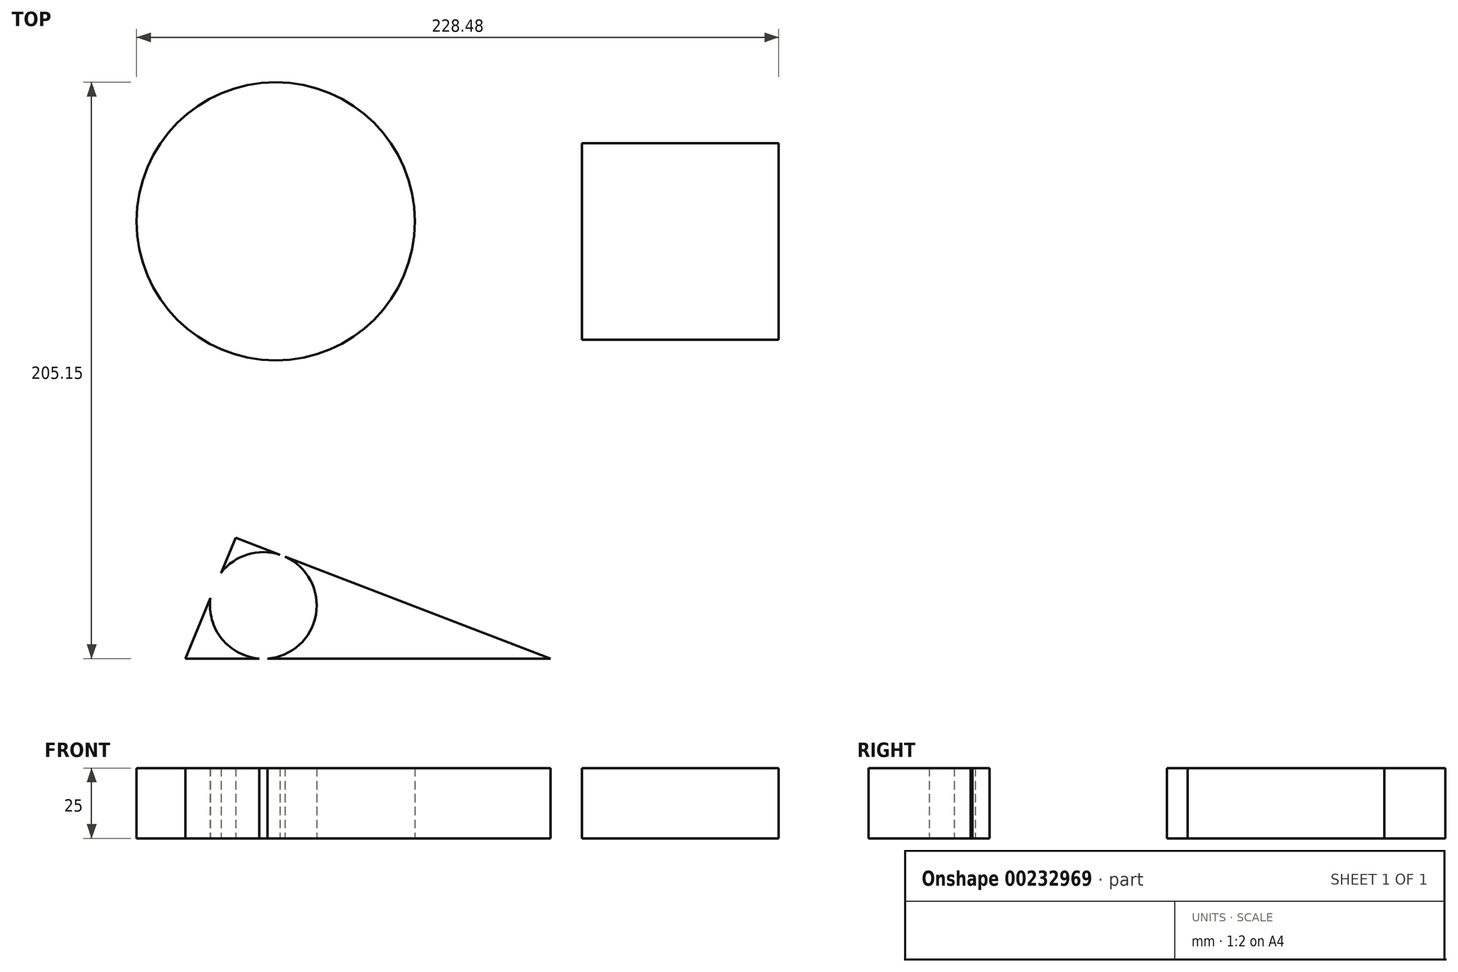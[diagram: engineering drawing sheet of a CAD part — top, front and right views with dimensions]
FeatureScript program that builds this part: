
annotation { "Feature Type Name" : "Feature", "Feature Type Description" : "" }
export const myFeature = defineFeature(function(context is Context, id is Id, definition is map)
    precondition{}
    {
        {
            var Q0;
            Q0=qCreatedBy(makeId("Top.planeOp"),FACE);
            var sketch = newSketch(context, id + "F0", { "sketchPlane" : qUnion([Q0])});
            skLineSegment(sketch, "E0.bottom", {"start": v(65.6, 3.6) * mm, "end": v(-4.4, 3.6) * mm});
            skLineSegment(sketch, "E0.top", {"start": v(65.6, 73.6) * mm, "end": v(-4.4, 73.6) * mm});
            skLineSegment(sketch, "E0.left", {"start": v(65.6, 3.6) * mm, "end": v(65.6, 73.6) * mm});
            skLineSegment(sketch, "E0.right", {"start": v(-4.4, 3.6) * mm, "end": v(-4.4, 73.6) * mm});
            skCircle(sketch, "E1", {"center": v(30.6, 38.6) * mm, "radius": 35 * mm});
            skPoint(sketch, "E1.first.point", {"position": v(30.6, 3.6) * mm});
            skPoint(sketch, "E1.second.point", {"position": v(30.6, 73.6) * mm});
            skPoint(sketch, "E1.third.point", {"position": v(65.6, 38.6) * mm});
            skLineSegment(sketch, "E2.bottom", {"start": v(-78.38, 10.8) * mm, "end": v(-148.38, 10.8) * mm});
            skLineSegment(sketch, "E2.top", {"start": v(-78.38, 80.8) * mm, "end": v(-148.38, 80.8) * mm});
            skLineSegment(sketch, "E2.left", {"start": v(-78.38, 10.8) * mm, "end": v(-78.38, 80.8) * mm});
            skLineSegment(sketch, "E2.right", {"start": v(-148.38, 10.8) * mm, "end": v(-148.38, 80.8) * mm});
            skCircle(sketch, "E3", {"center": v(-113.38, 45.8) * mm, "radius": 49.5 * mm});
            skLineSegment(sketch, "E4", {"start": v(-145.57, -109.85) * mm, "end": v(-15.57, -109.85) * mm});
            skLineSegment(sketch, "E5", {"start": v(-15.57, -109.85) * mm, "end": v(-127.6, -66.85) * mm});
            skLineSegment(sketch, "E6", {"start": v(-127.6, -66.85) * mm, "end": v(-145.57, -109.85) * mm});
            skCircle(sketch, "E7", {"center": v(-117.78, -90.92) * mm, "radius": 18.98 * mm});
            skPoint(sketch, "E7.first.point", {"position": v(-136.58, -88.35) * mm});
            skPoint(sketch, "E7.second.point", {"position": v(-98.92, -93.13) * mm});
            skPoint(sketch, "E7.third.point", {"position": v(-110.07, -73.57) * mm});
            skSolve(sketch);
        }
        {
            var Q0;
            {var subQ0=sQuery(id+"F0.wireOp",EDGE,"E2.left");Q0=makeQuery(id+"F0.imprint","IMPRINT",FACE,{"disambiguationData":[TD([[makeQuery(id+"F0.imprint","IMPRINT",EDGE,{"derivedFrom":subQ0}),-1.0]])]});}
            var Q1;
            {var subQ0=sQuery(id+"F0.wireOp",EDGE,"E2.right");Q1=makeQuery(id+"F0.imprint","IMPRINT",FACE,{"disambiguationData":[TD([[makeQuery(id+"F0.imprint","IMPRINT",EDGE,{"derivedFrom":subQ0}),1.0]])]});}
            var Q2;
            {var subQ0=sQuery(id+"F0.wireOp",EDGE,"E6");var subQ1=sQuery(id+"F0.wireOp",EDGE,"E4");var subQ2=makeQuery(id+"F0.imprint","INTERSECT",VERTEX,{"derivedFrom":[subQ1,subQ0]});Q2=makeQuery(id+"F0.imprint","IMPRINT",FACE,{"disambiguationData":[TD([[makeQuery(id+"F0.imprint","IMPRINT",EDGE,{"disambiguationData":[TD([[subQ2,-1.0]])],"derivedFrom":subQ1}),1.0]])]});}
            var Q3;
            {var subQ0=sQuery(id+"F0.wireOp",EDGE,"E5");var subQ1=sQuery(id+"F0.wireOp",EDGE,"E4");var subQ2=makeQuery(id+"F0.imprint","INTERSECT",VERTEX,{"derivedFrom":[subQ1,subQ0]});Q3=makeQuery(id+"F0.imprint","IMPRINT",FACE,{"disambiguationData":[TD([[makeQuery(id+"F0.imprint","IMPRINT",EDGE,{"disambiguationData":[TD([[subQ2,1.0]])],"derivedFrom":subQ1}),1.0]])]});}
            var Q4;
            {var subQ0=sQuery(id+"F0.wireOp",EDGE,"E6");var subQ1=sQuery(id+"F0.wireOp",EDGE,"E5");var subQ2=makeQuery(id+"F0.imprint","INTERSECT",VERTEX,{"derivedFrom":[subQ1,subQ0]});Q4=makeQuery(id+"F0.imprint","IMPRINT",FACE,{"disambiguationData":[TD([[makeQuery(id+"F0.imprint","IMPRINT",EDGE,{"disambiguationData":[TD([[subQ2,1.0]])],"derivedFrom":subQ1}),1.0]])]});}
            var Q5;
            {var subQ0=sQuery(id+"F0.wireOp",EDGE,"E0.right");var subQ1=sQuery(id+"F0.wireOp",EDGE,"E0.top");var subQ2=makeQuery(id+"F0.imprint","INTERSECT",VERTEX,{"derivedFrom":[subQ1,subQ0]});Q5=makeQuery(id+"F0.imprint","IMPRINT",FACE,{"disambiguationData":[TD([[makeQuery(id+"F0.imprint","IMPRINT",EDGE,{"disambiguationData":[TD([[subQ2,1.0]])],"derivedFrom":subQ1}),1.0]])]});}
            var Q6;
            {var subQ0=sQuery(id+"F0.wireOp",EDGE,"E0.left");var subQ1=sQuery(id+"F0.wireOp",EDGE,"E0.top");var subQ2=makeQuery(id+"F0.imprint","INTERSECT",VERTEX,{"derivedFrom":[subQ1,subQ0]});Q6=makeQuery(id+"F0.imprint","IMPRINT",FACE,{"disambiguationData":[TD([[makeQuery(id+"F0.imprint","IMPRINT",EDGE,{"disambiguationData":[TD([[subQ2,-1.0]])],"derivedFrom":subQ1}),1.0]])]});}
            var Q7;
            {var subQ0=sQuery(id+"F0.wireOp",EDGE,"E2.top");Q7=makeQuery(id+"F0.imprint","IMPRINT",FACE,{"disambiguationData":[TD([[makeQuery(id+"F0.imprint","IMPRINT",EDGE,{"derivedFrom":subQ0}),-1.0]])]});}
            var Q8;
            {var subQ0=sQuery(id+"F0.wireOp",EDGE,"E0.right");var subQ1=sQuery(id+"F0.wireOp",EDGE,"E0.bottom");var subQ2=makeQuery(id+"F0.imprint","INTERSECT",VERTEX,{"derivedFrom":[subQ1,subQ0]});Q8=makeQuery(id+"F0.imprint","IMPRINT",FACE,{"disambiguationData":[TD([[makeQuery(id+"F0.imprint","IMPRINT",EDGE,{"disambiguationData":[TD([[subQ2,1.0]])],"derivedFrom":subQ1}),-1.0]])]});}
            var Q9;
            {var subQ0=sQuery(id+"F0.wireOp",EDGE,"E0.left");var subQ1=sQuery(id+"F0.wireOp",EDGE,"E0.bottom");var subQ2=makeQuery(id+"F0.imprint","INTERSECT",VERTEX,{"derivedFrom":[subQ1,subQ0]});Q9=makeQuery(id+"F0.imprint","IMPRINT",FACE,{"disambiguationData":[TD([[makeQuery(id+"F0.imprint","IMPRINT",EDGE,{"disambiguationData":[TD([[subQ2,-1.0]])],"derivedFrom":subQ1}),-1.0]])]});}
            var Q10;
            {var subQ0=sQuery(id+"F0.wireOp",EDGE,"E2.bottom");Q10=makeQuery(id+"F0.imprint","IMPRINT",FACE,{"disambiguationData":[TD([[makeQuery(id+"F0.imprint","IMPRINT",EDGE,{"derivedFrom":subQ0}),1.0]])]});}
            var Q11;
            {var subQ0=sQuery(id+"F0.wireOp",EDGE,"E1");var subQ1=makeQuery(id+"F0.imprint","INTERSECT",VERTEX,{"derivedFrom":[sQuery(id+"F0.wireOp",EDGE,"E0.top"),subQ0]});Q11=makeQuery(id+"F0.imprint","IMPRINT",FACE,{"disambiguationData":[TD([[makeQuery(id+"F0.imprint","IMPRINT",EDGE,{"disambiguationData":[TD([[subQ1,1.0]])],"derivedFrom":subQ0}),1.0]])]});}
            var Q12;
            Q12=makeQuery(id+"F0.imprint","IMPRINT",FACE,{"disambiguationData":[TD([[makeQuery(id+"F0.imprint","IMPRINT",EDGE,{"derivedFrom":sQuery(id+"F0.wireOp",EDGE,"E2.bottom")}),-1.0]])]});
            var Q13;
            {var subQ0=sQuery(id+"F0.wireOp",EDGE,"E7");var subQ7=sQuery(id+"F0.wireOp",EDGE,"E4");var subQ8=makeQuery(id+"F0.imprint","INTERSECT",VERTEX,{"disambiguationData":[OD(0.0)],"derivedFrom":[subQ7,subQ0]});Q13=makeQuery(id+"F0.imprint","IMPRINT",FACE,{"disambiguationData":[TD([[makeQuery(id+"F0.imprint","IMPRINT",EDGE,{"disambiguationData":[TD([[subQ8,-1.0]])],"derivedFrom":subQ7}),1.0]])]});}
            var Q14;
            {var subQ0=sQuery(id+"F0.wireOp",EDGE,"E7");var subQ1=sQuery(id+"F0.wireOp",EDGE,"E4");var subQ2=makeQuery(id+"F0.imprint","INTERSECT",VERTEX,{"disambiguationData":[OD(0.0)],"derivedFrom":[subQ1,subQ0]});Q14=makeQuery(id+"F0.imprint","IMPRINT",FACE,{"disambiguationData":[TD([[makeQuery(id+"F0.imprint","IMPRINT",EDGE,{"disambiguationData":[TD([[subQ2,-1.0]])],"derivedFrom":subQ1}),-1.0]])]});}
            var Q15;
            {var subQ0=sQuery(id+"F0.wireOp",EDGE,"E7");var subQ1=sQuery(id+"F0.wireOp",EDGE,"E5");var subQ2=makeQuery(id+"F0.imprint","INTERSECT",VERTEX,{"disambiguationData":[OD(0.0)],"derivedFrom":[subQ1,subQ0]});Q15=makeQuery(id+"F0.imprint","IMPRINT",FACE,{"disambiguationData":[TD([[makeQuery(id+"F0.imprint","IMPRINT",EDGE,{"disambiguationData":[TD([[subQ2,-1.0]])],"derivedFrom":subQ1}),-1.0]])]});}
            var Q16;
            {var subQ0=sQuery(id+"F0.wireOp",EDGE,"E7");var subQ1=sQuery(id+"F0.wireOp",EDGE,"E6");var subQ2=makeQuery(id+"F0.imprint","INTERSECT",VERTEX,{"disambiguationData":[OD(0.0)],"derivedFrom":[subQ1,subQ0]});Q16=makeQuery(id+"F0.imprint","IMPRINT",FACE,{"disambiguationData":[TD([[makeQuery(id+"F0.imprint","IMPRINT",EDGE,{"disambiguationData":[TD([[subQ2,-1.0]])],"derivedFrom":subQ1}),-1.0]])]});}
            extrude(context, id + "F1", {"entities" : qUnion([Q0, Q1, Q2, Q3, Q4, Q5, Q6, Q7, Q8, Q9, Q10, Q11, Q12, Q13, Q14, Q15, Q16]), "depth" : 25 * mm});
        }
    });
